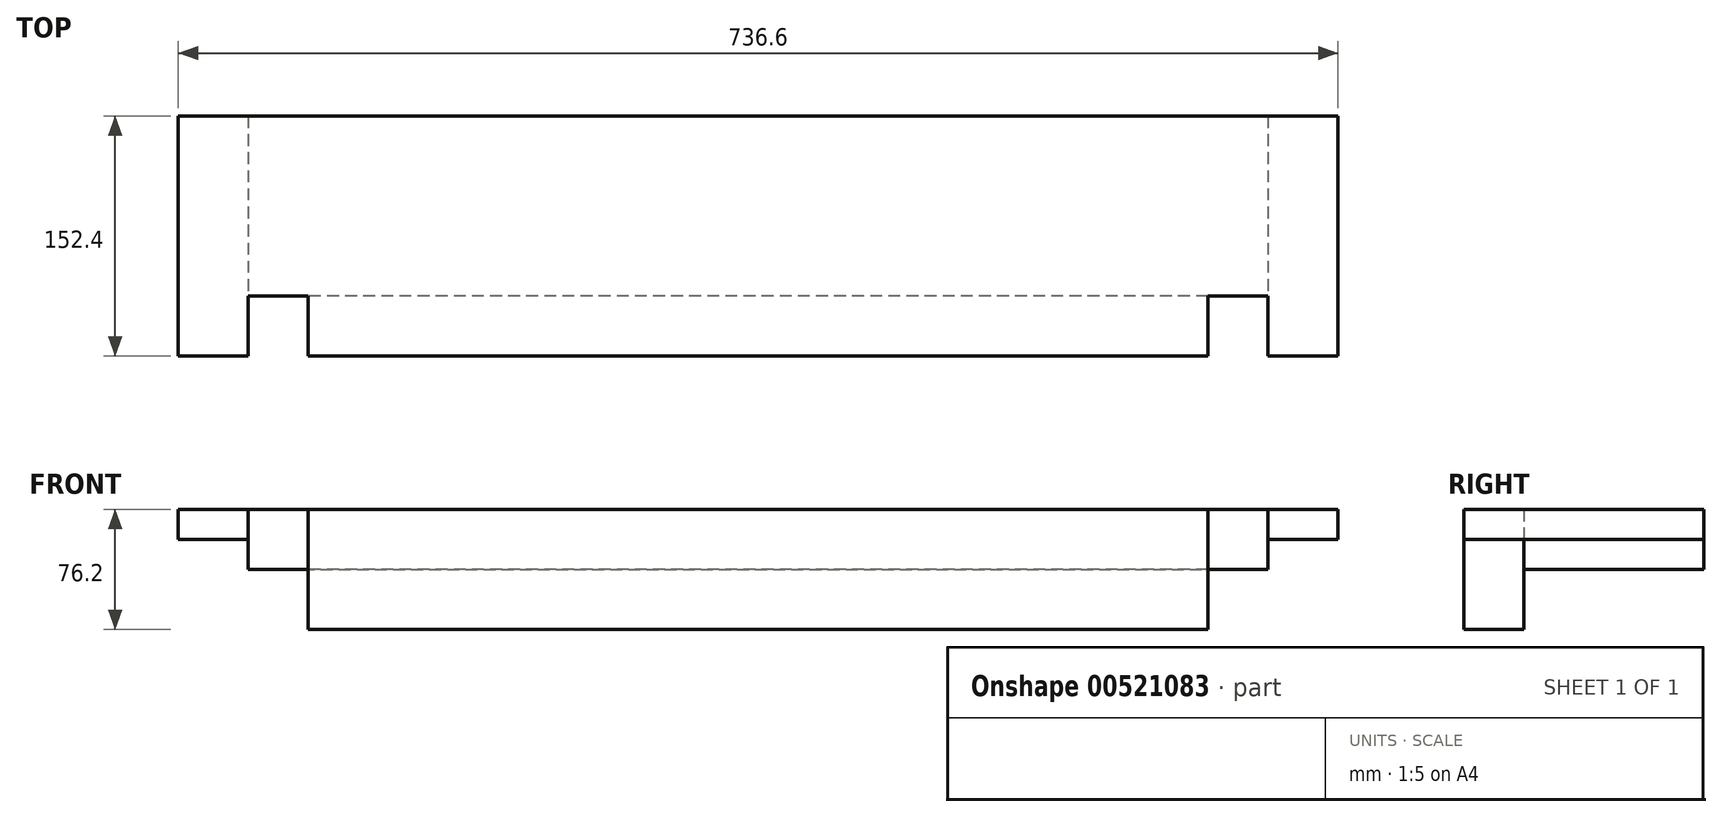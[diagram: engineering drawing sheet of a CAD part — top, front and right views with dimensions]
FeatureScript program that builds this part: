
annotation { "Feature Type Name" : "Feature", "Feature Type Description" : "" }
export const myFeature = defineFeature(function(context is Context, id is Id, definition is map)
    precondition{}
    {
        {
            var Q0;
            Q0=qCreatedBy(makeId("Front.planeOp"),FACE);
            var sketch = newSketch(context, id + "F0", { "sketchPlane" : qUnion([Q0])});
            skLineSegment(sketch, "E0", {"start": v(-368.3, 0) * mm, "end": v(368.3, 0) * mm, "construction": true});
            skLineSegment(sketch, "E1", {"start": v(0, 87.46) * mm, "end": v(0, -116.17) * mm, "construction": true});
            skLineSegment(sketch, "E2.bottom", {"start": v(-368.3, 19.05) * mm, "end": v(368.3, 19.05) * mm});
            skLineSegment(sketch, "E2.top", {"start": v(-368.3, -19.05) * mm, "end": v(368.3, -19.05) * mm});
            skLineSegment(sketch, "E2.left", {"start": v(-368.3, 19.05) * mm, "end": v(-368.3, -19.05) * mm});
            skLineSegment(sketch, "E2.right", {"start": v(368.3, 19.05) * mm, "end": v(368.3, -19.05) * mm});
            skSolve(sketch);
        }
        {
            var Q0;
            Q0 = qSketchRegion(id + "F0", true);
            extrude(context, id + "F1", {"entities" : qUnion([Q0]), "endBound" : BoundingType.SYMMETRIC, "depth" : 152.4 * mm, "offsetDistance" : 25.4 * mm});
        }
        {
            var Q0;
            Q0=makeQuery(id+"F1.opExtrude","CAP_FACE",FACE,{"disambiguationData":[OSD([sQuery(id+"F0.wireOp",EDGE,"E2.bottom"),sQuery(id+"F0.wireOp",EDGE,"E2.top"),sQuery(id+"F0.wireOp",EDGE,"E2.left"),sQuery(id+"F0.wireOp",EDGE,"E2.right")])],"isStart":false});
            var sketch = newSketch(context, id + "F2", { "sketchPlane" : qUnion([Q0])});
            skLineSegment(sketch, "E3", {"start": v(-368.3, 0) * mm, "end": v(368.3, 0) * mm, "construction": true});
            skLineSegment(sketch, "E4.bottom", {"start": v(-323.85, 0) * mm, "end": v(-368.3, 0) * mm});
            skLineSegment(sketch, "E4.top", {"start": v(-323.85, -19.05) * mm, "end": v(-368.3, -19.05) * mm});
            skLineSegment(sketch, "E4.left", {"start": v(-323.85, 0) * mm, "end": v(-323.85, -19.05) * mm});
            skLineSegment(sketch, "E4.right", {"start": v(-368.3, 0) * mm, "end": v(-368.3, -19.05) * mm});
            skLineSegment(sketch, "E5.bottom", {"start": v(323.85, 0) * mm, "end": v(368.3, 0) * mm});
            skLineSegment(sketch, "E5.top", {"start": v(323.85, -19.05) * mm, "end": v(368.3, -19.05) * mm});
            skLineSegment(sketch, "E5.left", {"start": v(323.85, 0) * mm, "end": v(323.85, -19.05) * mm});
            skLineSegment(sketch, "E5.right", {"start": v(368.3, 0) * mm, "end": v(368.3, -19.05) * mm});
            skSolve(sketch);
        }
        {
            var Q0;
            Q0 = qSketchRegion(id + "F2", true);
            extrude(context, id + "F3", {"entities" : qUnion([Q0]), "operationType" : NewBodyOperationType.REMOVE, "endBound" : BoundingType.THROUGH_ALL, "oppositeDirection" : true, "depth" : 25.4 * mm, "offsetDistance" : 25.4 * mm});
        }
        {
            var Q0;
            Q0=makeQuery(id+"F1.opExtrude","SWEPT_FACE",FACE,{"disambiguationData":[OSD([sQuery(id+"F0.wireOp",EDGE,"E2.top")])]});
            var sketch = newSketch(context, id + "F4", { "sketchPlane" : qUnion([Q0])});
            skLineSegment(sketch, "E6.0.0", {"start": v(-323.85, -76.2) * mm, "end": v(-323.85, 76.2) * mm});
            skLineSegment(sketch, "E6.0.1", {"start": v(-323.85, 76.2) * mm, "end": v(-368.3, 76.2) * mm});
            skLineSegment(sketch, "E6.0.2", {"start": v(-368.3, 76.2) * mm, "end": v(-368.3, -76.2) * mm});
            skLineSegment(sketch, "E6.0.3", {"start": v(-368.3, -76.2) * mm, "end": v(-323.85, -76.2) * mm});
            skLineSegment(sketch, "E7.0.0", {"start": v(-323.85, -76.2) * mm, "end": v(323.85, -76.2) * mm});
            skLineSegment(sketch, "E7.0.1", {"start": v(323.85, -76.2) * mm, "end": v(323.85, 76.2) * mm});
            skLineSegment(sketch, "E7.0.2", {"start": v(323.85, 76.2) * mm, "end": v(-323.85, 76.2) * mm});
            skLineSegment(sketch, "E7.0.3", {"start": v(-323.85, 76.2) * mm, "end": v(-323.85, -76.2) * mm});
            skLineSegment(sketch, "E8.0.0", {"start": v(323.85, -76.2) * mm, "end": v(368.3, -76.2) * mm});
            skLineSegment(sketch, "E8.0.1", {"start": v(368.3, -76.2) * mm, "end": v(368.3, 76.2) * mm});
            skLineSegment(sketch, "E8.0.2", {"start": v(368.3, 76.2) * mm, "end": v(323.85, 76.2) * mm});
            skLineSegment(sketch, "E8.0.3", {"start": v(323.85, 76.2) * mm, "end": v(323.85, -76.2) * mm});
            skLineSegment(sketch, "E9.bottom", {"start": v(-368.3, 76.2) * mm, "end": v(-285.75, 76.2) * mm});
            skLineSegment(sketch, "E9.top", {"start": v(-368.3, 38.1) * mm, "end": v(-285.75, 38.1) * mm});
            skLineSegment(sketch, "E9.left", {"start": v(-368.3, 76.2) * mm, "end": v(-368.3, 38.1) * mm});
            skLineSegment(sketch, "E9.right", {"start": v(-285.75, 76.2) * mm, "end": v(-285.75, 38.1) * mm});
            skLineSegment(sketch, "E10.bottom", {"start": v(368.3, 76.2) * mm, "end": v(285.75, 76.2) * mm});
            skLineSegment(sketch, "E10.top", {"start": v(368.3, 38.1) * mm, "end": v(285.75, 38.1) * mm});
            skLineSegment(sketch, "E10.left", {"start": v(368.3, 76.2) * mm, "end": v(368.3, 38.1) * mm});
            skLineSegment(sketch, "E10.right", {"start": v(285.75, 76.2) * mm, "end": v(285.75, 38.1) * mm});
            skSolve(sketch);
        }
        {
            var Q0;
            {var subQ5=sQuery(id+"F4.wireOp",EDGE,"E9.left");Q0=makeQuery(id+"F4.imprint","IMPRINT",FACE,{"disambiguationData":[TD([[makeQuery(id+"F4.imprint","IMPRINT",EDGE,{"derivedFrom":subQ5}),1.0]])]});}
            var Q1;
            {var subQ5=sQuery(id+"F4.wireOp",EDGE,"E9.right");Q1=makeQuery(id+"F4.imprint","IMPRINT",FACE,{"disambiguationData":[TD([[makeQuery(id+"F4.imprint","IMPRINT",EDGE,{"derivedFrom":subQ5}),-1.0]])]});}
            var Q2;
            {var subQ5=sQuery(id+"F4.wireOp",EDGE,"E10.right");Q2=makeQuery(id+"F4.imprint","IMPRINT",FACE,{"disambiguationData":[TD([[makeQuery(id+"F4.imprint","IMPRINT",EDGE,{"derivedFrom":subQ5}),1.0]])]});}
            var Q3;
            {var subQ5=sQuery(id+"F4.wireOp",EDGE,"E10.left");Q3=makeQuery(id+"F4.imprint","IMPRINT",FACE,{"disambiguationData":[TD([[makeQuery(id+"F4.imprint","IMPRINT",EDGE,{"derivedFrom":subQ5}),-1.0]])]});}
            extrude(context, id + "F5", {"entities" : qUnion([Q0, Q1, Q2, Q3]), "operationType" : NewBodyOperationType.REMOVE, "endBound" : BoundingType.THROUGH_ALL, "oppositeDirection" : true, "depth" : 25.4 * mm, "offsetDistance" : 25.4 * mm});
        }
        {
            var Q0;
            Q0=makeQuery(id+"F5.boolean.opBoolean","COPY",FACE,{"derivedFrom":makeQuery(id+"F5.opExtrude","SWEPT_FACE",FACE,{"disambiguationData":[OSD([sQuery(id+"F4.wireOp",EDGE,"E9.right")])]})});
            var sketch = newSketch(context, id + "F6", { "sketchPlane" : qUnion([Q0])});
            skLineSegment(sketch, "E11.bottom", {"start": v(38.1, -19.05) * mm, "end": v(76.2, -19.05) * mm});
            skLineSegment(sketch, "E11.top", {"start": v(38.1, -57.15) * mm, "end": v(76.2, -57.15) * mm});
            skLineSegment(sketch, "E11.left", {"start": v(38.1, -19.05) * mm, "end": v(38.1, -57.15) * mm});
            skLineSegment(sketch, "E11.right", {"start": v(76.2, -19.05) * mm, "end": v(76.2, -57.15) * mm});
            skSolve(sketch);
        }
        {
            var Q0;
            Q0 = qSketchRegion(id + "F6", true);
            var Q1;
            Q1=makeQuery(id+"F5.boolean.opBoolean","COPY",FACE,{"derivedFrom":makeQuery(id+"F5.opExtrude","SWEPT_FACE",FACE,{"disambiguationData":[OSD([sQuery(id+"F4.wireOp",EDGE,"E10.right")])]})});
            extrude(context, id + "F7", {"entities" : qUnion([Q0]), "operationType" : NewBodyOperationType.ADD, "endBound" : BoundingType.UP_TO_SURFACE, "oppositeDirection" : true, "depth" : 25.4 * mm, "endBoundEntityFace" : qUnion([Q1]), "offsetDistance" : 25.4 * mm});
        }
    });
